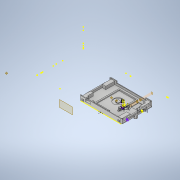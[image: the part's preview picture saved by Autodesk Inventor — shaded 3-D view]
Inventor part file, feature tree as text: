
AUTODESK INVENTOR PART (.ipt)
format: ipt  version: 2020 (Build 240168000, 168)  size: 5,346,816 bytes
history: native  units: mm
features: sketch x139, move_body x109, extrude x86, direct_edit x59, other x40, chamfer x10, split x1, draft x1, revolve x1, plane x1
ambient origin geometry x8: Origin, YZ Plane, XZ Plane, XY Plane, X Axis, Y Axis, Z Axis, Center Point
bodies: Solid1 (feature_tree), Solid2 (feature_tree)
feature tree (447):
  sketch  "Sketch1"  dims[d2=105.0mm d3=75.0mm d6=109.0mm]
  extrude  "Extrusion1"  Depth=109.0mm
  extrude  "Extrusion2"  Depth=7.0mm TaperAngle=0.0deg
  extrude  "Extrusion3"  Depth=2.5mm TaperAngle=0.0deg
  sketch  "Sketch6"  dims[d10=105.0mm d11=75.0mm d12=2.5mm d13=0.0mm]
  extrude  "Extrusion4"  Depth=19.5mm
  sketch  "Sketch8"  dims[d17=10.0mm d18=1.2mm d19=0.0mm]
  extrude  "Extrusion5"  Depth=1.2mm TaperAngle=0.0deg
  extrude  "Extrusion6"  Depth=30.0mm
  extrude  "Extrusion7"  Depth=60.0mm
  extrude  "Extrusion8"  Depth=1.0mm TaperAngle=0.0deg
  sketch  "Sketch14"  dims[d31=2.8mm d32=60.0mm]
  extrude  "Extrusion9"  Depth=20.0mm
  extrude  "Extrusion10"  Depth=0.5mm TaperAngle=0.0deg
  extrude  "Extrusion11"  Depth=12.5mm
  extrude  "Extrusion12"  Depth=10.0mm TaperAngle=0.0deg
  sketch  "Sketch17"  dims[d33=5.6mm d34=1.0mm d35=0.0mm]
  sketch  "Sketch18"  dims[d36=16.0mm d37=20.0mm]
  sketch  "Sketch19"  dims[d38=1.0mm d39=0.0mm d40=0.5mm d41=0.0mm]
  sketch  "Sketch20"  dims[d42=11.0mm d43=12.5mm]
  sketch  "Sketch21"  dims[d44=10.0mm d45=1.0mm d46=0.0mm]
  extrude  "Extrusion13"  Depth=2.0mm TaperAngle=0.0deg
  extrude  "Extrusion14"  Depth=15.0mm
  sketch  "Sketch22"  dims[d47=0.2mm d48=0.0mm d49=2.0mm d50=0.0mm]
  direct_edit  "Direct Edit1"
  direct_edit  "Direct Edit2"
  extrude  "Extrusion15"  Depth=70.0mm
  extrude  "Extrusion16"  Depth=58.0mm
  extrude  "Extrusion17"  Depth=2.0mm TaperAngle=0.0deg
  direct_edit  "Direct Edit3"
  direct_edit  "Direct Edit4"
  direct_edit  "Direct Edit5"
  extrude  "Extrusion18"  Depth=79.0mm
  extrude  "Extrusion19"  TaperAngle=0.0deg  [1 undecoded]
  extrude  "Extrusion20"  Depth=3.0mm TaperAngle=0.0deg
  extrude  "Extrusion21"  Depth=3.0mm
  direct_edit  "Direct Edit6"
  split  "Split1"
  move_body  "Move Body1"
  move_body  "Move Body2"
  move_body  "Move Body3"
  move_body  "Move Body4"
  move_body  "Move Body5"
  move_body  "Move Body6"
  sketch  "Sketch28"  dims[d63=2.5mm d64=0.0mm d65=0.0mm d66=0.0mm d67=-0.5mm]
  direct_edit  "Direct Edit7"
  sketch  "Sketch29"  dims[d68=0.0mm d69=0.0mm d70=1.0mm d71=3.0mm d72=0.0mm]
  extrude  "Extrusion22"  Depth=2.54mm
  extrude  "Extrusion23"  Depth=5.588mm
  sketch  "Sketch32"  dims[d84=11.176mm d85=5.588mm]
  direct_edit  "Direct Edit8"
  direct_edit  "Direct Edit9"
  extrude  "Extrusion24"  TaperAngle=0.0deg  [1 undecoded]
  direct_edit  "Direct Edit10"
  direct_edit  "Direct Edit11"
  direct_edit  "Direct Edit12"
  sketch  "Sketch33"  dims[d86=1.0mm d87=0.0mm d88=0.0mm d89=0.0mm d90=-47.25mm]
  direct_edit  "Direct Edit13"
  other  "Work Point1"
  sketch  "Sketch34"  dims[d91=0.0mm d92=0.0mm d93=-95.5mm d94=0.0mm d95=0.0mm d96=-0.6mm]
  other  "Work Point2"
  other  "Work Point3"
  sketch  "Sketch35"  dims[d101=27.7mm d102=48.2mm]
  extrude  "Extrusion25"  TaperAngle=0.0deg  [1 undecoded]
  extrude  "Extrusion26"  Depth=48.2mm
  direct_edit  "Direct Edit14"
  direct_edit  "Direct Edit15"
  extrude  "Extrusion27"  Depth=7.0mm
  extrude  "Extrusion28"  Depth=7.0mm
  direct_edit  "Direct Edit16"
  draft  "FaceDraft1"
  chamfer  "Chamfer1"  Distance=4.0mm
  chamfer  "Chamfer2"  Distance=3.0mm
  chamfer  "Chamfer3"  Distance=1.0mm
  direct_edit  "Direct Edit17"
  direct_edit  "Direct Edit18"
  extrude  "Extrusion29"  Depth=1.5mm TaperAngle=0.0deg
  extrude  "Extrusion30"  TaperAngle=0.0deg  [1 undecoded]
  extrude  "Extrusion31"  TaperAngle=180.0deg  [1 undecoded]
  sketch  "Sketch42"  dims[d121=9.75mm d122=12.75mm d123=244.0mm d124=-9.75mm d125=0.0mm d126=0.0mm]
  direct_edit  "Direct Edit19"
  sketch  "Sketch43"  dims[d127=180.0deg d128=180.0deg]
  direct_edit  "Direct Edit20"
  sketch  "Sketch44"  dims[d129=180.0deg d130=122.75mm d131=-19.25mm d132=0.0mm]
  extrude  "Extrusion32"  Depth=122.75mm TaperAngle=0.0deg
  direct_edit  "Direct Edit21"
  extrude  "Extrusion33"  Depth=5.0mm
  extrude  "Extrusion34"  Depth=5.0mm
  sketch  "Sketch48"  dims[d141=5.0mm d142=5.0mm]
  sketch  "Sketch49"  dims[d143=5.0mm d144=2.0mm]
  extrude  "Extrusion35"  Depth=5.0mm
  sketch  "Sketch51"  dims[d147=2.0mm d148=1.0mm d149=0.0mm]
  extrude  "Extrusion36"  Depth=5.0mm
  extrude  "Extrusion37"  Depth=2.0mm
  move_body  "Move Body7"
  move_body  "Move Body8"
  move_body  "Move Body9"
  move_body  "Move Body10"
  move_body  "Move Body11"
  move_body  "Move Body12"
  sketch  "Sketch53"  dims[d152=5.0mm d153=5.0mm]
  direct_edit  "Direct Edit22"
  extrude  "Extrusion38"  Depth=2.0mm
  sketch  "Sketch54"  dims[d154=5.0mm d155=5.0mm]
  sketch  "Sketch55"  dims[d156=5.0mm d157=5.0mm]
  sketch  "Sketch56"  dims[d158=3.0mm d159=3.0mm]
  extrude  "Extrusion39"  Depth=1.0mm TaperAngle=0.0deg
  direct_edit  "Direct Edit23"
  sketch  "Sketch58"  dims[d162=3.0mm d163=0.0mm d164=11.0mm]
  direct_edit  "Direct Edit24"
  extrude  "Extrusion40"  Depth=5.0mm
  direct_edit  "Direct Edit25"
  extrude  "Extrusion41"  Depth=5.0mm
  direct_edit  "Direct Edit26"
  direct_edit  "Direct Edit27"
  direct_edit  "Direct Edit28"
  direct_edit  "Direct Edit29"
  extrude  "Extrusion42"  Depth=5.0mm
  extrude  "Extrusion43"  Depth=5.0mm
  direct_edit  "Direct Edit30"
  sketch  "Sketch62"  dims[d171=11.0mm d172=0.0mm d173=0.0mm d174=1.0mm]
  extrude  "Extrusion44"  Depth=3.0mm
  direct_edit  "Direct Edit31"
  direct_edit  "Direct Edit32"
  extrude  "Extrusion45"  Depth=3.0mm
  move_body  "Move Body13"
  move_body  "Move Body14"
  move_body  "Move Body15"
  move_body  "Move Body16"
  extrude  "Extrusion46"  Depth=11.0mm
  sketch  "Sketch66"  dims[d192=0.0mm d193=0.0mm d194=1.0mm d195=12.5mm]
  direct_edit  "Direct Edit33"
  sketch  "Sketch67"  dims[d196=5.0mm d198=2.1mm]
  direct_edit  "Direct Edit34"
  extrude  "Extrusion47"  Depth=11.0mm
  direct_edit  "Direct Edit35"
  move_body  "Move Body17"
  direct_edit  "Direct Edit36"
  direct_edit  "Direct Edit37"
  direct_edit  "Direct Edit38"
  direct_edit  "Direct Edit39"
  direct_edit  "Direct Edit40"
  direct_edit  "Direct Edit41"
  extrude  "Extrusion48"  Depth=11.0mm
  extrude  "Extrusion49"  Depth=11.0mm
  extrude  "Extrusion50"  Depth=1.0mm TaperAngle=0.0deg
  sketch  "Sketch72"  dims[d213=5.0mm d214=0.0mm d215=0.6mm]
  revolve  "Revolution1"  [1 undecoded]
  sketch  "Sketch74"  dims[d218=5.0mm d219=0.0mm d220=0.0mm d221=0.0mm d222=-0.2mm]
  sketch  "Sketch75"  dims[d223=0.0mm d224=0.0mm d225=0.2mm d226=30.0deg]
  plane  "Work Plane1"
  extrude  "Extrusion51"  Depth=1.0mm TaperAngle=0.0deg
  direct_edit  "Direct Edit42"
  sketch  "Sketch77"  dims[d233=1.07845mm d234=2.0mm d235=45.0deg d236=0.0mm d237=0.0mm d238=-0.5mm]
  extrude  "Extrusion52"  TaperAngle=0.0deg  [1 undecoded]
  extrude  "Extrusion53"  Depth=12.5mm
  extrude  "Extrusion54"  Depth=2.1mm
  extrude  "Extrusion55"  Depth=10.0mm
  direct_edit  "Direct Edit43"
  direct_edit  "Direct Edit44"
  extrude  "Extrusion56"  TaperAngle=0.0deg  [1 undecoded]
  extrude  "Extrusion57"  Depth=0.6mm
  extrude  "Extrusion58"  Depth=13.7mm
  extrude  "Extrusion59"  Depth=0.6mm
  extrude  "Extrusion60"  Depth=13.7mm
  extrude  "Extrusion61"  TaperAngle=0.0deg  [1 undecoded]
  direct_edit  "Direct Edit45"
  direct_edit  "Direct Edit46"
  direct_edit  "Direct Edit47"
  extrude  "Extrusion62"  TaperAngle=30.0deg  [1 undecoded]
  direct_edit  "Direct Edit48"
  sketch  "Sketch89"  dims[d286=163.5mm d287=0.0mm d288=79.0mm d289=-132.0mm d290=0.0mm d291=2.0mm]
  extrude  "Extrusion63"  Depth=0.8mm TaperAngle=45.0deg
  extrude  "Extrusion64"  TaperAngle=0.0deg  [1 undecoded]
  extrude  "Extrusion65"  Depth=0.6mm TaperAngle=0.0deg
  extrude  "Extrusion66"  Depth=7.5mm
  extrude  "Extrusion67"  Depth=17.5mm
  sketch  "Sketch95"  dims[d309=180.0deg d310=1.0mm d311=0.0mm]
  sketch  "Sketch96"  dims[d312=0.0mm d313=0.0mm d314=-1.0mm d315=15.0mm]
  extrude  "Extrusion68"  Depth=1.0mm TaperAngle=0.0deg
  direct_edit  "Direct Edit49"
  direct_edit  "Direct Edit50"
  direct_edit  "Direct Edit51"
  extrude  "Extrusion69"  Depth=1.2mm
  extrude  "Extrusion70"  Depth=1.2mm TaperAngle=0.0deg
  direct_edit  "Direct Edit52"
  extrude  "Extrusion71"  Depth=2.0mm TaperAngle=0.0deg
  direct_edit  "Direct Edit53"
  direct_edit  "Direct Edit54"
  sketch  "Sketch100"  dims[d320=15.0mm]
  extrude  "Extrusion72"  Depth=23.0mm
  direct_edit  "Direct Edit55"
  direct_edit  "Direct Edit56"
  direct_edit  "Direct Edit57"
  direct_edit  "Direct Edit58"
  direct_edit  "Direct Edit59"
  chamfer  "Chamfer4"  Distance=1.2mm
  chamfer  "Chamfer5"  Distance=1.0mm
  chamfer  "Chamfer6"  Distance=2.0mm
  sketch  "스케치102"
  sketch  "3D 스케치1"
  sketch  "3D 스케치2"
  sketch  "3D 스케치3"
  sketch  "스케치103"
  sketch  "3D 스케치4"
  sketch  "3D 스케치5"
  sketch  "3D 스케치6"
  extrude  "돌출73"  Depth=4.75mm TaperAngle=0.0deg
  other  "분할2"
  other  "본체 이동18"
  other  "본체 이동19"
  sketch  "스케치105"
  sketch  "스케치106"
  extrude  "돌출74"  Depth=2.0mm TaperAngle=0.0deg
  extrude  "돌출75"  Depth=8.5mm TaperAngle=0.0deg
  sketch  "스케치109"
  other  "본체 이동20"
  sketch  "스케치110"
  sketch  "스케치111"
  extrude  "돌출76"  Depth=17.8mm
  sketch  "스케치113"
  sketch  "스케치114"
  extrude  "돌출77"  Depth=35.6mm
  other  "본체 이동21"
  sketch  "스케치115"
  sketch  "스케치116"
  sketch  "스케치117"
  sketch  "스케치118"
  sketch  "스케치119"
  sketch  "스케치120"
  extrude  "돌출78"  Depth=1.0mm TaperAngle=0.0deg
  other  "본체 이동22"
  sketch  "스케치121"
  sketch  "스케치122"
  sketch  "스케치123"
  sketch  "스케치124"
  sketch  "스케치125"
  sketch  "스케치126"
  sketch  "스케치127"
  other  "본체 이동23"
  extrude  "돌출79"  Depth=12.0mm
  extrude  "돌출80"  Depth=1.0mm TaperAngle=0.0deg
  sketch  "스케치130"
  extrude  "돌출81"  Depth=15.0mm
  extrude  "돌출82"  Depth=15.0mm
  chamfer  "모따기7"  Distance=13.0mm
  chamfer  "모따기8"  Distance=2.25mm
  chamfer  "모따기9"  Distance=2.0mm
  chamfer  "모따기10"  Distance=2.0mm
  other  "본체 이동24"
  other  "본체 이동25"
  other  "본체 이동26"
  other  "본체 이동27"
  other  "본체 이동28"
  other  "본체 이동29"
  other  "본체 이동30"
  other  "본체 이동31"
  other  "본체 이동32"
  other  "본체 이동33"
  sketch  "스케치133"
  other  "분할3"
  other  "분할4"
  other  "본체 이동34"
  other  "분할5"
  other  "본체 이동35"
  other  "결합1"
  other  "결합2"
  other  "결합3"
  extrude  "돌출83"  Depth=8.0mm TaperAngle=0.0deg
  sketch  "스케치137"
  other  "본체 이동36"
  extrude  "돌출84"  Depth=2.5mm TaperAngle=0.0deg
  sketch  "스케치138"
  sketch  "스케치139"
  sketch  "스케치140"
  extrude  "돌출85"  Depth=2.5mm TaperAngle=0.0deg
  extrude  "돌출86"  Depth=8.0mm TaperAngle=0.0deg
  sketch  "Sketch5"  dims[d7=79.0mm d8=7.0mm d9=0.0mm]
  sketch  "Sketch7"  dims[d14=5.0mm d15=0.0mm d16=19.5mm]
  sketch  "Sketch11"  dims[d28=1.0mm d29=0.0mm d30=30.0mm]
  sketch  "Sketch23"  dims[d51=2.0mm d52=0.0mm d53=15.0mm]
  sketch  "Sketch24"  dims[d54=9.0mm d55=70.0mm]
  sketch  "Sketch25"  dims[d56=46.5mm d57=58.0mm]
  sketch  "Sketch26"  dims[d58=39.0mm d59=2.0mm d60=0.0mm]
  sketch  "Sketch27"  dims[d61=109.0mm d62=79.0mm]
  sketch  "Sketch30"  dims[d73=1.0mm d74=0.0mm d79=3.0mm]
  sketch  "Sketch31"  dims[d82=4.5mm d83=2.54mm]
  sketch  "Sketch36"  dims[d103=68.2mm d104=7.0mm]
  sketch  "Sketch37"  dims[d105=5.5mm d106=7.0mm]
  sketch  "Sketch38"  dims[d107=5.5mm]
  sketch  "Sketch39"  dims[d108=7.0mm]
  sketch  "Sketch40"  dims[d109=5.5mm d110=4.0mm d111=0.0mm d112=3.0mm d113=0.0mm d114=1.0mm d115=0.0mm]
  sketch  "Sketch41"  dims[d116=1.0mm d117=0.0mm d118=0.0mm d119=0.0mm d120=1.5mm]
  sketch  "Sketch45"  dims[d133=0.0mm d134=0.0mm d135=-1.0mm d136=5.0mm]
  sketch  "Sketch46"  dims[d137=5.0mm d138=5.0mm]
  sketch  "Sketch47"  dims[d139=5.0mm d140=5.0mm]
  sketch  "Sketch50"  dims[d145=2.0mm d146=2.0mm]
  sketch  "Sketch52"  dims[d150=5.0mm d151=5.0mm]
  sketch  "Sketch57"  dims[d160=3.0mm d161=3.0mm]
  sketch  "Sketch59"  dims[d165=11.0mm d166=11.0mm]
  sketch  "Sketch60"  dims[d167=11.0mm d168=11.0mm]
  sketch  "Sketch61"  dims[d169=11.0mm d170=11.0mm]
  sketch  "Sketch63"  dims[d175=0.0mm d176=0.0mm d177=1.0mm d178=2.0mm d179=0.0mm]
  sketch  "Sketch64"  dims[d180=0.0mm d181=0.0mm d182=1.0mm d183=0.0mm d184=0.0mm d185=1.0mm]
  sketch  "Sketch65"  dims[d186=0.0mm d187=0.0mm d188=-5.0mm d189=-5.0mm d190=0.0mm d191=0.0mm]
  sketch  "Sketch68"  dims[d199=10.0mm d200=0.0mm d201=10.0mm]
  sketch  "Sketch69"  dims[d202=0.5mm d203=0.0mm d204=0.0mm d205=0.0mm d206=-0.75mm]
  sketch  "Sketch70"  dims[d207=0.0mm d208=0.0mm d209=2.75mm d210=0.6mm]
  sketch  "Sketch71"  dims[d211=3.05mm d212=13.7mm]
  sketch  "Sketch73"  dims[d216=2.7mm d217=13.7mm]
  sketch  "Sketch76"  dims[d227=1.0mm d228=2.0mm d229=45.0deg d230=0.8mm d231=2.0mm d232=45.0deg]
  sketch  "Sketch78"  dims[d239=0.0mm d240=0.0mm d241=-1.25mm d242=0.6mm d243=0.0mm]
  sketch  "Sketch79"  dims[d244=1.0mm d245=0.0mm d246=7.5mm]
  sketch  "Sketch80"  dims[d247=20.0mm d248=17.5mm]
  sketch  "Sketch81"  dims[d249=17.5mm d250=1.0mm d251=0.0mm]
  sketch  "Sketch82"  dims[d254=0.0mm d255=0.0mm d256=1.2mm d257=3.0mm]
  sketch  "Sketch83"  dims[d258=0.0mm d259=0.0mm d260=-2.0mm d261=1.2mm d262=0.0mm]
  sketch  "Sketch84"  dims[d263=0.0mm d264=0.0mm d265=-0.5mm d266=2.0mm d267=0.0mm]
  sketch  "Sketch85"  dims[d268=1.0mm d269=0.0mm d271=23.0mm]
  sketch  "Sketch86"  dims[d272=9.8mm d273=1.2mm d274=0.0mm]
  sketch  "Sketch87"  dims[d275=8.8mm d276=1.0mm d277=0.0mm d278=2.0mm d279=0.0mm]
  sketch  "Sketch88"  dims[d280=2.0mm d281=0.0mm d282=-117.25mm d283=4.75mm d284=0.0mm d285=-118.0mm]
  sketch  "Sketch90"  dims[d292=165.25mm d293=0.0mm d294=78.0mm d295=0.0mm d296=8.5mm d297=0.0mm]
  sketch  "Sketch91"  dims[d298=3.7mm d299=17.8mm]
  sketch  "Sketch92"  dims[d300=20.6mm d301=35.6mm]
  sketch  "Sketch93"  dims[d302=0.0mm d303=0.0mm d304=0.75mm d305=1.0mm d306=0.0mm]
  sketch  "Sketch94"  dims[d307=13.0mm d308=12.0mm]
  sketch  "Sketch97"  dims[d316=15.0mm d317=15.0mm]
  sketch  "Sketch98"  dims[d318=15.0mm]
  sketch  "Sketch99"  dims[d319=15.0mm]
  sketch  "Sketch101"  dims[d321=15.0mm d322=13.0mm d323=0.0mm d324=0.0mm d325=2.25mm d326=0.0mm d327=0.0mm d328=2.0mm d329=0.0mm d330=0.0mm d331=2.0mm d332=4.5mm d333=0.0mm d334=0.0mm d335=0.0mm d336=2.5mm d337=0.0mm d338=0.0mm d339=2.5mm d340=2.0mm d341=0.0mm d342=0.0mm d343=0.0mm d344=54.0mm d345=0.0mm d346=0.0mm d347=0.25mm d348=0.0mm d349=0.0mm d350=-0.25mm d351=0.0mm d352=0.0mm d353=2.75mm d354=0.0mm d355=0.0mm d356=-0.01583mm d357=4.0mm d358=0.0mm d359=15.3mm d360=15.3mm d361=13.3mm d362=15.3mm d363=13.3mm d364=15.3mm d365=13.3mm d366=4.5mm d367=0.0mm d368=0.0mm d369=0.0mm d370=-2.1mm d371=4.5mm d372=0.0mm d373=0.0mm d374=0.0mm d375=-2.4mm d376=0.0mm d377=0.0mm d378=-0.25mm d379=0.0mm d380=0.0mm d381=2.5mm d382=0.0mm d383=0.0mm d384=1.25mm d385=6.0mm d386=6.0mm d387=6.0mm d388=6.0mm d389=1.0mm d390=0.0mm d391=180.0deg d392=180.0deg d393=99.75mm d394=0.0mm d395=-79.25mm d396=0.0mm d397=-6.0mm d398=0.0mm d399=0.6mm d400=0.0mm d401=0.0mm d402=5.0mm d403=0.0mm d404=0.0mm d405=0.0mm d406=1.0mm d407=25.2mm d408=20.6mm d409=1.0mm d410=0.0mm d411=0.0mm d412=0.0mm d413=0.5mm d414=0.0mm d415=33.75mm d416=1.25mm d417=0.0mm d418=0.0mm d419=-0.3mm d420=0.0mm d421=0.0mm d422=-0.3mm d423=0.0mm d424=0.0mm d425=-0.3mm d426=0.0mm d427=0.0mm d428=-0.3mm d429=0.0mm d430=0.0mm d431=-0.3mm d432=0.0mm d433=0.0mm d434=-0.3mm d435=0.0mm d436=0.0mm d437=-0.3mm d438=0.0mm d439=0.0mm d440=-0.3mm d441=0.0mm d442=0.0mm d443=-0.5mm d444=0.0mm d445=0.0mm d446=-0.3mm d447=0.0mm d448=0.0mm d449=-0.3mm d450=0.0mm d451=0.0mm d452=-0.3mm d453=0.0mm d454=0.0mm d455=-0.3mm d456=0.0mm d457=0.0mm d458=-0.5mm d459=0.0mm d460=0.0mm d461=-1.0mm d462=0.0mm d463=0.0mm d464=-1.5mm d465=0.0mm d466=0.0mm d467=0.3mm d468=2.0mm d469=1.0mm d470=0.0mm d471=0.6mm d472=0.0mm d473=0.6mm d474=0.0mm d475=4.5mm d476=4.0mm d477=45.0deg d478=-4.5mm d479=5.0mm d480=5.0mm d481=3.0mm d482=0.0mm d483=0.0mm d484=0.0mm d485=-16.5mm d486=3.75mm d487=0.0mm d488=8.0mm d489=0.0mm d490=8.0mm d491=8.0mm d492=8.0mm d493=8.0mm d494=9.0mm d495=9.0mm d496=9.0mm d497=9.0mm d498=8.0mm d499=0.0mm d500=8.0mm d501=1.0mm d502=8.0mm d503=1.0mm d504=8.0mm d505=1.4mm d506=1.0mm d507=8.0mm d508=1.0mm d509=8.0mm d510=0.0mm d511=0.0mm d512=0.0mm d513=-0.2mm d514=0.0mm d515=0.0mm d516=-0.2mm d517=0.0mm d518=0.0mm d519=-1.2mm d520=3.0mm d521=3.0mm d522=2.0mm d523=0.0mm d524=1.5mm d525=1.5mm d526=3.0mm d527=0.0mm d528=1.0mm d529=1.0mm d530=3.0mm d531=0.0mm d532=3.0mm d533=3.0mm d534=2.0mm d535=0.0mm d536=1.5mm d537=1.5mm d538=3.0mm d539=0.0mm d540=1.0mm d541=1.0mm d542=3.0mm d543=0.0mm d544=0.0mm d545=0.0mm d546=0.05mm d547=0.0mm d548=0.0mm d549=0.05mm d550=0.0mm d551=0.0mm d552=1.25mm d553=3.0mm d554=3.0mm d555=111.0mm d556=0.0mm d557=0.0mm d558=0.0mm d559=-0.2mm d560=0.0mm d561=0.0mm d562=-0.2mm d563=3.5mm d564=0.0mm d565=3.5mm d566=0.0mm d567=5.0mm d568=0.0mm d569=5.0mm d570=0.0mm d571=2.2mm d572=2.2mm d573=3.0mm d574=0.0mm d575=2.2mm d576=2.2mm d577=3.0mm d578=0.0mm d579=0.0mm d580=0.0mm d581=3.8mm d582=0.0mm d583=0.0mm d584=-3.35mm d585=0.0mm d586=0.0mm d587=-3.35mm d588=0.0mm d589=0.0mm d590=3.8mm d591=0.0mm d592=0.0mm d593=1.5mm d594=0.0mm d595=0.0mm d596=1.5mm d597=0.0mm d598=0.0mm d599=1.5mm d600=0.0mm d601=0.0mm d602=1.5mm d603=6.0mm d604=6.0mm d605=1.5mm d606=0.0mm d607=6.0mm d608=6.0mm d609=1.5mm d610=0.0mm d611=0.0mm d612=0.0mm d613=14.0mm d614=14.0mm d615=0.0mm d616=0.0mm d617=0.0mm d618=14.0mm d619=0.0mm d620=0.0mm d621=14.0mm d622=0.0mm d623=0.0mm d624=-0.75mm d625=14.0mm d626=2.0mm d627=0.0mm d628=0.0mm d629=0.0mm d630=-0.25mm d631=0.0mm d632=0.0mm d633=-0.25mm d634=-0.5mm d635=0.0mm d636=0.0mm d637=0.0mm d638=0.0mm d639=-0.25mm d640=0.0mm d641=0.0mm d642=-0.25mm d643=0.0mm d644=0.0mm d645=-0.25mm d646=0.0mm d647=0.0mm d648=-0.25mm d649=0.0mm d650=0.0mm d651=-0.25mm d652=0.0mm d653=0.0mm d654=-0.25mm d655=0.0mm d656=0.0mm d657=-0.25mm d658=0.0mm d659=0.0mm d660=-0.5mm d661=2.0mm d662=2.0mm d663=45.0deg d664=2.0mm d665=2.0mm d666=45.0deg d667=2.0mm d668=2.0mm d669=45.0deg d670=5.0mm d671=30.0mm d672=0.0mm d673=39.75mm d674=48.0mm d675=3.0mm d676=105.25mm d677=-48.25mm d678=-81.25mm d679=3.5mm d680=8.0mm d681=0.0mm d682=5.0mm d683=17.0mm d684=0.0mm d685=114.0mm d686=-1.75mm d687=0.0mm d688=12.3mm d689=7.25mm d690=5.05mm d691=12.75mm d693=1.0mm d695=1.0mm d696=7.0mm d697=0.0mm d698=14.25mm d699=0.0mm d700=-1.75mm d701=1.25mm d702=0.0mm d703=54.5mm d704=0.0mm d705=0.0mm d706=33.4mm d707=1.5mm d708=0.75mm d709=0.0mm d710=0.0mm d711=-0.3mm d712=55.0mm d713=0.0mm d714=5.520407mm d716=3.0mm d717=6.5mm d718=0.0mm d719=6.5mm d720=0.0mm d721=3.0mm d722=3.5mm d723=0.0mm d724=1.75mm d725=2.0mm d726=45.0deg d727=1.75mm d728=2.0mm d729=45.0deg d730=1.75mm d731=2.0mm d732=45.0deg d733=1.75mm d734=2.0mm d735=45.0deg d736=10.0mm d737=0.0mm d738=0.0mm d739=10.0mm d740=0.0mm d741=0.0mm d742=180.0deg d743=-10.0mm d744=-12.4mm d745=-78.5mm d746=9.75mm d747=0.0mm d748=-0.5mm d749=-10.0mm d750=0.0mm d751=-0.05mm d752=0.0mm d753=-4.5mm d754=0.0mm d755=0.0mm d756=4.5mm d757=0.0mm d758=180.0deg d759=0.0mm d760=0.0mm d761=5.0mm d762=0.0mm d763=0.0mm d764=13.0mm d765=0.0mm d766=0.0mm d767=13.0mm d768=3.5mm d769=0.0mm d770=10.0mm d771=0.0mm d772=0.0mm d773=5.25mm d774=0.0mm d775=2.499988mm d776=2.5mm d777=55.0mm d778=0.0mm d779=8.0mm d780=0.0mm]
  other  "작업 평면3"
  sketch  "스케치104"
  sketch  "스케치107"
  sketch  "스케치108"
  sketch  "스케치112"
  sketch  "스케치128"
  sketch  "스케치129"
  sketch  "스케치131"
  sketch  "스케치132"
  sketch  "스케치134"
  sketch  "스케치135"
  sketch  "스케치136"
  sketch  "스케치141"
  sketch  "스케치142"
  other  "복합1"
  move_body  "Move1"
  move_body  "Move2"
  move_body  "Move3"
  move_body  "Move4"
  move_body  "Move5"
  move_body  "Move6"
  move_body  "Move7"
  move_body  "Move8"
  move_body  "Move9"
  move_body  "Move10"
  move_body  "Move11"
  move_body  "Move12"
  move_body  "Move13"
  move_body  "Move14"
  move_body  "Move15"
  move_body  "Move16"
  move_body  "Move17"
  move_body  "Move18"
  move_body  "Move19"
  move_body  "Move20"
  move_body  "Move21"
  move_body  "Move22"
  move_body  "Move23"
  move_body  "Move24"
  move_body  "Move25"
  move_body  "Move26"
  move_body  "Move27"
  move_body  "Move28"
  move_body  "Move29"
  move_body  "Move30"
  move_body  "Move31"
  move_body  "Move32"
  move_body  "Move33"
  move_body  "Move34"
  move_body  "Move35"
  move_body  "Move36"
  move_body  "Move37"
  move_body  "Move38"
  move_body  "Move39"
  move_body  "Move40"
  move_body  "Move41"
  move_body  "Move42"
  move_body  "Move43"
  move_body  "Move44"
  move_body  "Move45"
  move_body  "Move46"
  move_body  "Move47"
  move_body  "Move48"
  move_body  "Move49"
  move_body  "Move50"
  move_body  "Move51"
  move_body  "Move52"
  move_body  "Move53"
  move_body  "Move54"
  move_body  "Move55"
  move_body  "Move56"
  move_body  "Move57"
  move_body  "Move58"
  move_body  "Move59"
  move_body  "Move60"
  move_body  "Move61"
  move_body  "Move62"
  move_body  "Move63"
  move_body  "Move64"
  move_body  "Move65"
  move_body  "Move66"
  move_body  "Move67"
  move_body  "Move68"
  move_body  "Move69"
  move_body  "Move70"
  move_body  "Move71"
  move_body  "Move72"
  move_body  "Move73"
  move_body  "Move74"
  move_body  "Move75"
  move_body  "Move76"
  move_body  "Move77"
  move_body  "Move78"
  move_body  "Move79"
  move_body  "Move80"
  move_body  "Move81"
  move_body  "Move82"
  move_body  "Move83"
  move_body  "Move84"
  move_body  "Move85"
  move_body  "Move86"
  move_body  "Move87"
  move_body  "Move88"
  move_body  "Move89"
  move_body  "Move90"
  move_body  "Move91"
  move_body  "Move92"
  other  "솔리드4"
  other  "솔리드5"
  other  "Srf1"
  other  "솔리드6"
  other  "솔리드7"
  other  "솔리드8"
  other  "솔리드9"
  other  "솔리드10"
  other  "솔리드11"
note: 11 required parameter values undecoded (feature->parameter linkage not recoverable at this tier; creation-order binding heuristic only, values carry confidence <= 0.55)